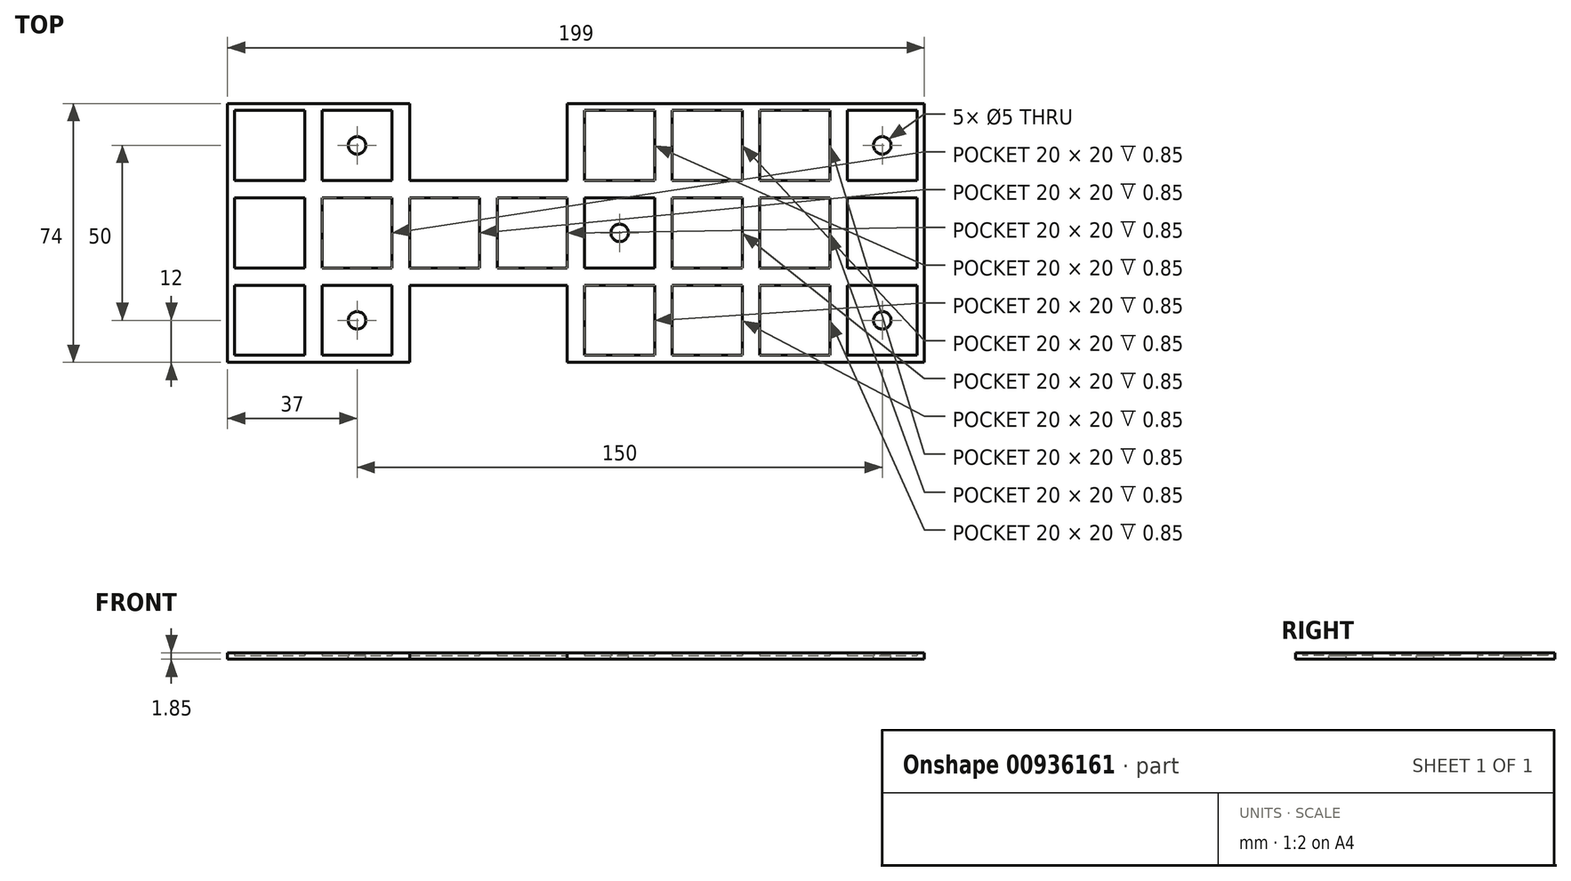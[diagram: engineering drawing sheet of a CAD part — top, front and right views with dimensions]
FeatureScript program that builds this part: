
annotation { "Feature Type Name" : "Feature", "Feature Type Description" : "" }
export const myFeature = defineFeature(function(context is Context, id is Id, definition is map)
    precondition{}
    {
        {
            var Q0;
            Q0=qCreatedBy(makeId("Top.planeOp"),FACE);
            var sketch = newSketch(context, id + "F0", { "sketchPlane" : qUnion([Q0])});
            skLineSegment(sketch, "E0.bottom", {"start": v(0, 0) * mm, "end": v(20, 0) * mm});
            skLineSegment(sketch, "E0.top", {"start": v(0, -20) * mm, "end": v(20, -20) * mm});
            skLineSegment(sketch, "E0.left", {"start": v(0, 0) * mm, "end": v(0, -20) * mm});
            skLineSegment(sketch, "E0.right", {"start": v(20, 0) * mm, "end": v(20, -20) * mm});
            skLineSegment(sketch, "E1.0.1.0", {"start": v(0, 25) * mm, "end": v(20, 25) * mm});
            skLineSegment(sketch, "E1.0.1.1", {"start": v(0, 25) * mm, "end": v(0, 5) * mm});
            skLineSegment(sketch, "E1.0.1.2", {"start": v(20, 25) * mm, "end": v(20, 5) * mm});
            skLineSegment(sketch, "E1.0.1.3", {"start": v(0, 5) * mm, "end": v(20, 5) * mm});
            skLineSegment(sketch, "E1.0.2.0", {"start": v(0, 50) * mm, "end": v(20, 50) * mm});
            skLineSegment(sketch, "E1.0.2.1", {"start": v(0, 50) * mm, "end": v(0, 30) * mm});
            skLineSegment(sketch, "E1.0.2.2", {"start": v(20, 50) * mm, "end": v(20, 30) * mm});
            skLineSegment(sketch, "E1.0.2.3", {"start": v(0, 30) * mm, "end": v(20, 30) * mm});
            skLineSegment(sketch, "E1.1.0.0", {"start": v(-25, 0) * mm, "end": v(-5, 0) * mm});
            skLineSegment(sketch, "E1.1.0.1", {"start": v(-25, 0) * mm, "end": v(-25, -20) * mm});
            skLineSegment(sketch, "E1.1.0.2", {"start": v(-5, 0) * mm, "end": v(-5, -20) * mm});
            skLineSegment(sketch, "E1.1.0.3", {"start": v(-25, -20) * mm, "end": v(-5, -20) * mm});
            skLineSegment(sketch, "E1.1.1.0", {"start": v(-25, 25) * mm, "end": v(-5, 25) * mm});
            skLineSegment(sketch, "E1.1.1.1", {"start": v(-25, 25) * mm, "end": v(-25, 5) * mm});
            skLineSegment(sketch, "E1.1.1.2", {"start": v(-5, 25) * mm, "end": v(-5, 5) * mm});
            skLineSegment(sketch, "E1.1.1.3", {"start": v(-25, 5) * mm, "end": v(-5, 5) * mm});
            skLineSegment(sketch, "E1.1.2.0", {"start": v(-25, 50) * mm, "end": v(-5, 50) * mm});
            skLineSegment(sketch, "E1.1.2.1", {"start": v(-25, 50) * mm, "end": v(-25, 30) * mm});
            skLineSegment(sketch, "E1.1.2.2", {"start": v(-5, 50) * mm, "end": v(-5, 30) * mm});
            skLineSegment(sketch, "E1.1.2.3", {"start": v(-25, 30) * mm, "end": v(-5, 30) * mm});
            skLineSegment(sketch, "E1.2.0.0", {"start": v(-50, 0) * mm, "end": v(-30, 0) * mm});
            skLineSegment(sketch, "E1.2.0.1", {"start": v(-50, 0) * mm, "end": v(-50, -20) * mm});
            skLineSegment(sketch, "E1.2.0.2", {"start": v(-30, 0) * mm, "end": v(-30, -20) * mm});
            skLineSegment(sketch, "E1.2.0.3", {"start": v(-50, -20) * mm, "end": v(-30, -20) * mm});
            skLineSegment(sketch, "E1.2.1.0", {"start": v(-50, 25) * mm, "end": v(-30, 25) * mm});
            skLineSegment(sketch, "E1.2.1.1", {"start": v(-50, 25) * mm, "end": v(-50, 5) * mm});
            skLineSegment(sketch, "E1.2.1.2", {"start": v(-30, 25) * mm, "end": v(-30, 5) * mm});
            skLineSegment(sketch, "E1.2.1.3", {"start": v(-50, 5) * mm, "end": v(-30, 5) * mm});
            skLineSegment(sketch, "E1.2.2.0", {"start": v(-50, 50) * mm, "end": v(-30, 50) * mm});
            skLineSegment(sketch, "E1.2.2.1", {"start": v(-50, 50) * mm, "end": v(-50, 30) * mm});
            skLineSegment(sketch, "E1.2.2.2", {"start": v(-30, 50) * mm, "end": v(-30, 30) * mm});
            skLineSegment(sketch, "E1.2.2.3", {"start": v(-50, 30) * mm, "end": v(-30, 30) * mm});
            skLineSegment(sketch, "E1.3.0.0", {"start": v(-75, 0) * mm, "end": v(-55, 0) * mm});
            skLineSegment(sketch, "E1.3.0.1", {"start": v(-75, 0) * mm, "end": v(-75, -20) * mm});
            skLineSegment(sketch, "E1.3.0.2", {"start": v(-55, 0) * mm, "end": v(-55, -20) * mm});
            skLineSegment(sketch, "E1.3.0.3", {"start": v(-75, -20) * mm, "end": v(-55, -20) * mm});
            skLineSegment(sketch, "E1.3.1.0", {"start": v(-75, 25) * mm, "end": v(-55, 25) * mm});
            skLineSegment(sketch, "E1.3.1.1", {"start": v(-75, 25) * mm, "end": v(-75, 5) * mm});
            skLineSegment(sketch, "E1.3.1.2", {"start": v(-55, 25) * mm, "end": v(-55, 5) * mm});
            skLineSegment(sketch, "E1.3.1.3", {"start": v(-75, 5) * mm, "end": v(-55, 5) * mm});
            skLineSegment(sketch, "E1.3.2.0", {"start": v(-75, 50) * mm, "end": v(-55, 50) * mm});
            skLineSegment(sketch, "E1.3.2.1", {"start": v(-75, 50) * mm, "end": v(-75, 30) * mm});
            skLineSegment(sketch, "E1.3.2.2", {"start": v(-55, 50) * mm, "end": v(-55, 30) * mm});
            skLineSegment(sketch, "E1.3.2.3", {"start": v(-75, 30) * mm, "end": v(-55, 30) * mm});
            skLineSegment(sketch, "E1.4.1.0", {"start": v(-100, 25) * mm, "end": v(-80, 25) * mm});
            skLineSegment(sketch, "E1.4.1.1", {"start": v(-100, 25) * mm, "end": v(-100, 5) * mm});
            skLineSegment(sketch, "E1.4.1.2", {"start": v(-80, 25) * mm, "end": v(-80, 5) * mm});
            skLineSegment(sketch, "E1.4.1.3", {"start": v(-100, 5) * mm, "end": v(-80, 5) * mm});
            skLineSegment(sketch, "E1.5.1.0", {"start": v(-125, 25) * mm, "end": v(-105, 25) * mm});
            skLineSegment(sketch, "E1.5.1.1", {"start": v(-125, 25) * mm, "end": v(-125, 5) * mm});
            skLineSegment(sketch, "E1.5.1.2", {"start": v(-105, 25) * mm, "end": v(-105, 5) * mm});
            skLineSegment(sketch, "E1.5.1.3", {"start": v(-125, 5) * mm, "end": v(-105, 5) * mm});
            skLineSegment(sketch, "E1.6.0.0", {"start": v(-150, 0) * mm, "end": v(-130, 0) * mm});
            skLineSegment(sketch, "E1.6.0.1", {"start": v(-150, 0) * mm, "end": v(-150, -20) * mm});
            skLineSegment(sketch, "E1.6.0.2", {"start": v(-130, 0) * mm, "end": v(-130, -20) * mm});
            skLineSegment(sketch, "E1.6.0.3", {"start": v(-150, -20) * mm, "end": v(-130, -20) * mm});
            skLineSegment(sketch, "E1.6.1.0", {"start": v(-150, 25) * mm, "end": v(-130, 25) * mm});
            skLineSegment(sketch, "E1.6.1.1", {"start": v(-150, 25) * mm, "end": v(-150, 5) * mm});
            skLineSegment(sketch, "E1.6.1.2", {"start": v(-130, 25) * mm, "end": v(-130, 5) * mm});
            skLineSegment(sketch, "E1.6.1.3", {"start": v(-150, 5) * mm, "end": v(-130, 5) * mm});
            skLineSegment(sketch, "E1.6.2.0", {"start": v(-150, 50) * mm, "end": v(-130, 50) * mm});
            skLineSegment(sketch, "E1.6.2.1", {"start": v(-150, 50) * mm, "end": v(-150, 30) * mm});
            skLineSegment(sketch, "E1.6.2.2", {"start": v(-130, 50) * mm, "end": v(-130, 30) * mm});
            skLineSegment(sketch, "E1.6.2.3", {"start": v(-150, 30) * mm, "end": v(-130, 30) * mm});
            skLineSegment(sketch, "E1.7.0.0", {"start": v(-175, 0) * mm, "end": v(-155, 0) * mm});
            skLineSegment(sketch, "E1.7.0.1", {"start": v(-175, 0) * mm, "end": v(-175, -20) * mm});
            skLineSegment(sketch, "E1.7.0.2", {"start": v(-155, 0) * mm, "end": v(-155, -20) * mm});
            skLineSegment(sketch, "E1.7.0.3", {"start": v(-175, -20) * mm, "end": v(-155, -20) * mm});
            skLineSegment(sketch, "E1.7.1.0", {"start": v(-175, 25) * mm, "end": v(-155, 25) * mm});
            skLineSegment(sketch, "E1.7.1.1", {"start": v(-175, 25) * mm, "end": v(-175, 5) * mm});
            skLineSegment(sketch, "E1.7.1.2", {"start": v(-155, 25) * mm, "end": v(-155, 5) * mm});
            skLineSegment(sketch, "E1.7.1.3", {"start": v(-175, 5) * mm, "end": v(-155, 5) * mm});
            skLineSegment(sketch, "E1.7.2.0", {"start": v(-175, 50) * mm, "end": v(-155, 50) * mm});
            skLineSegment(sketch, "E1.7.2.1", {"start": v(-175, 50) * mm, "end": v(-175, 30) * mm});
            skLineSegment(sketch, "E1.7.2.2", {"start": v(-155, 50) * mm, "end": v(-155, 30) * mm});
            skLineSegment(sketch, "E1.7.2.3", {"start": v(-175, 30) * mm, "end": v(-155, 30) * mm});
            skLineSegment(sketch, "E1.direction1", {"start": v(0, 0) * mm, "end": v(-25, 0) * mm, "construction": true});
            skLineSegment(sketch, "E1.direction2", {"start": v(0, 0) * mm, "end": v(0, 25) * mm, "construction": true});
            skLineSegment(sketch, "E2.bottom", {"start": v(-177, 52) * mm, "end": v(22, 52) * mm});
            skLineSegment(sketch, "E2.top", {"start": v(-177, -22) * mm, "end": v(22, -22) * mm});
            skLineSegment(sketch, "E2.left", {"start": v(-177, 52) * mm, "end": v(-177, -22) * mm});
            skLineSegment(sketch, "E2.right", {"start": v(22, 52) * mm, "end": v(22, -22) * mm});
            skLineSegment(sketch, "E3.bottom", {"start": v(-125, -22) * mm, "end": v(-80, -22) * mm});
            skLineSegment(sketch, "E3.top", {"start": v(-125, 0) * mm, "end": v(-80, 0) * mm});
            skLineSegment(sketch, "E3.left", {"start": v(-125, -22) * mm, "end": v(-125, 0) * mm});
            skLineSegment(sketch, "E3.right", {"start": v(-80, -22) * mm, "end": v(-80, 0) * mm});
            skLineSegment(sketch, "E4.bottom", {"start": v(-125, 52) * mm, "end": v(-80, 52) * mm});
            skLineSegment(sketch, "E4.top", {"start": v(-125, 30) * mm, "end": v(-80, 30) * mm});
            skLineSegment(sketch, "E4.left", {"start": v(-125, 52) * mm, "end": v(-125, 30) * mm});
            skLineSegment(sketch, "E4.right", {"start": v(-80, 52) * mm, "end": v(-80, 30) * mm});
            skPoint(sketch, "E5", {"position": v(10, -10) * mm});
            skPoint(sketch, "E5.positionSnap0", {"position": v(10, 0) * mm});
            skPoint(sketch, "E5.positionSnap1", {"position": v(20, -10) * mm});
            skPoint(sketch, "E6", {"position": v(10, 40) * mm});
            skPoint(sketch, "E6.positionSnap0", {"position": v(20, 40) * mm});
            skPoint(sketch, "E6.positionSnap1", {"position": v(10, 50) * mm});
            skPoint(sketch, "E7", {"position": v(-65, 15) * mm});
            skPoint(sketch, "E7.positionSnap0", {"position": v(-50, 15) * mm});
            skPoint(sketch, "E7.positionSnap1", {"position": v(-65, 25) * mm});
            skPoint(sketch, "E8", {"position": v(-140, -10) * mm});
            skPoint(sketch, "E8.positionSnap0", {"position": v(-140, 0) * mm});
            skPoint(sketch, "E8.positionSnap1", {"position": v(-130, -10) * mm});
            skPoint(sketch, "E9", {"position": v(-140, 40) * mm});
            skPoint(sketch, "E9.positionSnap0", {"position": v(-130, 40) * mm});
            skPoint(sketch, "E9.positionSnap1", {"position": v(-140, 50) * mm});
            skSolve(sketch);
        }
        {
            var Q0;
            Q0=makeQuery(id+"F0.imprint","IMPRINT",FACE,{"disambiguationData":[TD([[makeQuery(id+"F0.imprint","IMPRINT",EDGE,{"derivedFrom":sQuery(id+"F0.wireOp",EDGE,"E0.bottom")}),1.0]])]});
            extrude(context, id + "F1", {"entities" : qUnion([Q0]), "depth" : .85 * mm, "offsetDistance" : 25 * mm});
        }
        {
            var Q0;
            Q0=makeQuery(id+"F0.imprint","IMPRINT",FACE,{"disambiguationData":[TD([[makeQuery(id+"F0.imprint","IMPRINT",EDGE,{"derivedFrom":sQuery(id+"F0.wireOp",EDGE,"E1.6.1.0")}),-1.0]])]});
            var Q1;
            Q1=makeQuery(id+"F0.imprint","IMPRINT",FACE,{"disambiguationData":[TD([[makeQuery(id+"F0.imprint","IMPRINT",EDGE,{"derivedFrom":sQuery(id+"F0.wireOp",EDGE,"E1.7.1.0")}),-1.0]])]});
            var Q2;
            Q2=makeQuery(id+"F0.imprint","IMPRINT",FACE,{"disambiguationData":[TD([[makeQuery(id+"F0.imprint","IMPRINT",EDGE,{"derivedFrom":sQuery(id+"F0.wireOp",EDGE,"E1.7.2.0")}),-1.0]])]});
            var Q3;
            Q3=makeQuery(id+"F0.imprint","IMPRINT",FACE,{"disambiguationData":[TD([[makeQuery(id+"F0.imprint","IMPRINT",EDGE,{"derivedFrom":sQuery(id+"F0.wireOp",EDGE,"E1.6.2.0")}),-1.0]])]});
            var Q4;
            Q4=makeQuery(id+"F0.imprint","IMPRINT",FACE,{"disambiguationData":[TD([[makeQuery(id+"F0.imprint","IMPRINT",EDGE,{"derivedFrom":sQuery(id+"F0.wireOp",EDGE,"E1.5.1.0")}),-1.0]])]});
            var Q5;
            Q5=makeQuery(id+"F0.imprint","IMPRINT",FACE,{"disambiguationData":[TD([[makeQuery(id+"F0.imprint","IMPRINT",EDGE,{"derivedFrom":sQuery(id+"F0.wireOp",EDGE,"E1.6.0.0")}),-1.0]])]});
            var Q6;
            Q6=makeQuery(id+"F0.imprint","IMPRINT",FACE,{"disambiguationData":[TD([[makeQuery(id+"F0.imprint","IMPRINT",EDGE,{"derivedFrom":sQuery(id+"F0.wireOp",EDGE,"E1.7.0.0")}),-1.0]])]});
            var Q7;
            Q7=makeQuery(id+"F0.imprint","IMPRINT",FACE,{"disambiguationData":[TD([[makeQuery(id+"F0.imprint","IMPRINT",EDGE,{"derivedFrom":sQuery(id+"F0.wireOp",EDGE,"E1.4.1.0")}),-1.0]])]});
            var Q8;
            Q8=makeQuery(id+"F0.imprint","IMPRINT",FACE,{"disambiguationData":[TD([[makeQuery(id+"F0.imprint","IMPRINT",EDGE,{"derivedFrom":sQuery(id+"F0.wireOp",EDGE,"E1.3.2.0")}),-1.0]])]});
            var Q9;
            Q9=makeQuery(id+"F0.imprint","IMPRINT",FACE,{"disambiguationData":[TD([[makeQuery(id+"F0.imprint","IMPRINT",EDGE,{"derivedFrom":sQuery(id+"F0.wireOp",EDGE,"E1.3.1.0")}),-1.0]])]});
            var Q10;
            Q10=makeQuery(id+"F0.imprint","IMPRINT",FACE,{"disambiguationData":[TD([[makeQuery(id+"F0.imprint","IMPRINT",EDGE,{"derivedFrom":sQuery(id+"F0.wireOp",EDGE,"E1.2.1.0")}),-1.0]])]});
            var Q11;
            Q11=makeQuery(id+"F0.imprint","IMPRINT",FACE,{"disambiguationData":[TD([[makeQuery(id+"F0.imprint","IMPRINT",EDGE,{"derivedFrom":sQuery(id+"F0.wireOp",EDGE,"E1.3.0.0")}),-1.0]])]});
            var Q12;
            Q12=makeQuery(id+"F0.imprint","IMPRINT",FACE,{"disambiguationData":[TD([[makeQuery(id+"F0.imprint","IMPRINT",EDGE,{"derivedFrom":sQuery(id+"F0.wireOp",EDGE,"E1.2.0.0")}),-1.0]])]});
            var Q13;
            Q13=makeQuery(id+"F0.imprint","IMPRINT",FACE,{"disambiguationData":[TD([[makeQuery(id+"F0.imprint","IMPRINT",EDGE,{"derivedFrom":sQuery(id+"F0.wireOp",EDGE,"E1.2.2.0")}),-1.0]])]});
            var Q14;
            Q14=makeQuery(id+"F0.imprint","IMPRINT",FACE,{"disambiguationData":[TD([[makeQuery(id+"F0.imprint","IMPRINT",EDGE,{"derivedFrom":sQuery(id+"F0.wireOp",EDGE,"E1.1.2.0")}),-1.0]])]});
            var Q15;
            Q15=makeQuery(id+"F0.imprint","IMPRINT",FACE,{"disambiguationData":[TD([[makeQuery(id+"F0.imprint","IMPRINT",EDGE,{"derivedFrom":sQuery(id+"F0.wireOp",EDGE,"E1.1.1.0")}),-1.0]])]});
            var Q16;
            Q16=makeQuery(id+"F0.imprint","IMPRINT",FACE,{"disambiguationData":[TD([[makeQuery(id+"F0.imprint","IMPRINT",EDGE,{"derivedFrom":sQuery(id+"F0.wireOp",EDGE,"E1.1.0.0")}),-1.0]])]});
            var Q17;
            Q17=makeQuery(id+"F0.imprint","IMPRINT",FACE,{"disambiguationData":[TD([[makeQuery(id+"F0.imprint","IMPRINT",EDGE,{"derivedFrom":sQuery(id+"F0.wireOp",EDGE,"E0.bottom")}),-1.0]])]});
            var Q18;
            Q18=makeQuery(id+"F0.imprint","IMPRINT",FACE,{"disambiguationData":[TD([[makeQuery(id+"F0.imprint","IMPRINT",EDGE,{"derivedFrom":sQuery(id+"F0.wireOp",EDGE,"E1.0.1.0")}),-1.0]])]});
            var Q19;
            Q19=makeQuery(id+"F0.imprint","IMPRINT",FACE,{"disambiguationData":[TD([[makeQuery(id+"F0.imprint","IMPRINT",EDGE,{"derivedFrom":sQuery(id+"F0.wireOp",EDGE,"E1.0.2.0")}),-1.0]])]});
            var Q20;
            Q20=makeQuery(id+"F1.opExtrude","CAP_FACE",FACE,{"disambiguationData":[OSD([sQuery(id+"F0.wireOp",EDGE,"E0.bottom"),sQuery(id+"F0.wireOp",EDGE,"E0.top"),sQuery(id+"F0.wireOp",EDGE,"E0.left"),sQuery(id+"F0.wireOp",EDGE,"E0.right"),sQuery(id+"F0.wireOp",EDGE,"E1.0.1.0"),sQuery(id+"F0.wireOp",EDGE,"E1.0.1.1"),sQuery(id+"F0.wireOp",EDGE,"E1.0.1.2"),sQuery(id+"F0.wireOp",EDGE,"E1.0.1.3"),sQuery(id+"F0.wireOp",EDGE,"E1.0.2.0"),sQuery(id+"F0.wireOp",EDGE,"E1.0.2.1"),sQuery(id+"F0.wireOp",EDGE,"E1.0.2.2"),sQuery(id+"F0.wireOp",EDGE,"E1.0.2.3"),sQuery(id+"F0.wireOp",EDGE,"E1.1.0.0"),sQuery(id+"F0.wireOp",EDGE,"E1.1.0.1"),sQuery(id+"F0.wireOp",EDGE,"E1.1.0.2"),sQuery(id+"F0.wireOp",EDGE,"E1.1.0.3"),sQuery(id+"F0.wireOp",EDGE,"E1.1.1.0"),sQuery(id+"F0.wireOp",EDGE,"E1.1.1.1"),sQuery(id+"F0.wireOp",EDGE,"E1.1.1.2"),sQuery(id+"F0.wireOp",EDGE,"E1.1.1.3"),sQuery(id+"F0.wireOp",EDGE,"E1.1.2.0"),sQuery(id+"F0.wireOp",EDGE,"E1.1.2.1"),sQuery(id+"F0.wireOp",EDGE,"E1.1.2.2"),sQuery(id+"F0.wireOp",EDGE,"E1.1.2.3"),sQuery(id+"F0.wireOp",EDGE,"E1.2.0.0"),sQuery(id+"F0.wireOp",EDGE,"E1.2.0.1"),sQuery(id+"F0.wireOp",EDGE,"E1.2.0.2"),sQuery(id+"F0.wireOp",EDGE,"E1.2.0.3"),sQuery(id+"F0.wireOp",EDGE,"E1.2.1.0"),sQuery(id+"F0.wireOp",EDGE,"E1.2.1.1"),sQuery(id+"F0.wireOp",EDGE,"E1.2.1.2"),sQuery(id+"F0.wireOp",EDGE,"E1.2.1.3"),sQuery(id+"F0.wireOp",EDGE,"E1.2.2.0"),sQuery(id+"F0.wireOp",EDGE,"E1.2.2.1"),sQuery(id+"F0.wireOp",EDGE,"E1.2.2.2"),sQuery(id+"F0.wireOp",EDGE,"E1.2.2.3"),sQuery(id+"F0.wireOp",EDGE,"E1.3.0.0"),sQuery(id+"F0.wireOp",EDGE,"E1.3.0.1"),sQuery(id+"F0.wireOp",EDGE,"E1.3.0.2"),sQuery(id+"F0.wireOp",EDGE,"E1.3.0.3"),sQuery(id+"F0.wireOp",EDGE,"E1.3.1.0"),sQuery(id+"F0.wireOp",EDGE,"E1.3.1.1"),sQuery(id+"F0.wireOp",EDGE,"E1.3.1.2"),sQuery(id+"F0.wireOp",EDGE,"E1.3.1.3"),sQuery(id+"F0.wireOp",EDGE,"E1.3.2.0"),sQuery(id+"F0.wireOp",EDGE,"E1.3.2.1"),sQuery(id+"F0.wireOp",EDGE,"E1.3.2.2"),sQuery(id+"F0.wireOp",EDGE,"E1.3.2.3"),sQuery(id+"F0.wireOp",EDGE,"E1.4.1.0"),sQuery(id+"F0.wireOp",EDGE,"E1.4.1.1"),sQuery(id+"F0.wireOp",EDGE,"E1.4.1.2"),sQuery(id+"F0.wireOp",EDGE,"E1.4.1.3"),sQuery(id+"F0.wireOp",EDGE,"E1.5.1.0"),sQuery(id+"F0.wireOp",EDGE,"E1.5.1.1"),sQuery(id+"F0.wireOp",EDGE,"E1.5.1.2"),sQuery(id+"F0.wireOp",EDGE,"E1.5.1.3"),sQuery(id+"F0.wireOp",EDGE,"E1.6.0.0"),sQuery(id+"F0.wireOp",EDGE,"E1.6.0.1"),sQuery(id+"F0.wireOp",EDGE,"E1.6.0.2"),sQuery(id+"F0.wireOp",EDGE,"E1.6.0.3"),sQuery(id+"F0.wireOp",EDGE,"E1.6.1.0"),sQuery(id+"F0.wireOp",EDGE,"E1.6.1.1"),sQuery(id+"F0.wireOp",EDGE,"E1.6.1.2"),sQuery(id+"F0.wireOp",EDGE,"E1.6.1.3"),sQuery(id+"F0.wireOp",EDGE,"E1.6.2.0"),sQuery(id+"F0.wireOp",EDGE,"E1.6.2.1"),sQuery(id+"F0.wireOp",EDGE,"E1.6.2.2"),sQuery(id+"F0.wireOp",EDGE,"E1.6.2.3"),sQuery(id+"F0.wireOp",EDGE,"E1.7.0.0"),sQuery(id+"F0.wireOp",EDGE,"E1.7.0.1"),sQuery(id+"F0.wireOp",EDGE,"E1.7.0.2"),sQuery(id+"F0.wireOp",EDGE,"E1.7.0.3"),sQuery(id+"F0.wireOp",EDGE,"E1.7.1.0"),sQuery(id+"F0.wireOp",EDGE,"E1.7.1.1"),sQuery(id+"F0.wireOp",EDGE,"E1.7.1.2"),sQuery(id+"F0.wireOp",EDGE,"E1.7.1.3"),sQuery(id+"F0.wireOp",EDGE,"E1.7.2.0"),sQuery(id+"F0.wireOp",EDGE,"E1.7.2.1"),sQuery(id+"F0.wireOp",EDGE,"E1.7.2.2"),sQuery(id+"F0.wireOp",EDGE,"E1.7.2.3"),sQuery(id+"F0.wireOp",EDGE,"E2.bottom"),sQuery(id+"F0.wireOp",EDGE,"E2.top"),sQuery(id+"F0.wireOp",EDGE,"E2.left"),sQuery(id+"F0.wireOp",EDGE,"E2.right"),sQuery(id+"F0.wireOp",EDGE,"E3.top"),sQuery(id+"F0.wireOp",EDGE,"E3.left"),sQuery(id+"F0.wireOp",EDGE,"E3.right"),sQuery(id+"F0.wireOp",EDGE,"E4.top"),sQuery(id+"F0.wireOp",EDGE,"E4.left"),sQuery(id+"F0.wireOp",EDGE,"E4.right")])],"isStart":false});
            var Q21;
            Q21=makeQuery(id+"F0.imprint","IMPRINT",FACE,{"disambiguationData":[TD([[makeQuery(id+"F0.imprint","IMPRINT",EDGE,{"derivedFrom":sQuery(id+"F0.wireOp",EDGE,"E0.bottom")}),1.0]])]});
            extrude(context, id + "F2", {"entities" : qUnion([Q0, Q1, Q2, Q3, Q4, Q5, Q6, Q7, Q8, Q9, Q10, Q11, Q12, Q13, Q14, Q15, Q16, Q17, Q18, Q19, Q20, Q21]), "operationType" : NewBodyOperationType.ADD, "oppositeDirection" : true, "depth" : 1 * mm, "offsetDistance" : 25 * mm});
        }
        {
            var Q0;
            Q0=sQuery(id+"F0.wireOp",VERTEX,"E9");
            var Q1;
            Q1=sQuery(id+"F0.wireOp",VERTEX,"E8");
            var Q2;
            Q2=sQuery(id+"F0.wireOp",VERTEX,"E7");
            var Q3;
            Q3=sQuery(id+"F0.wireOp",VERTEX,"E5");
            var Q4;
            Q4=sQuery(id+"F0.wireOp",VERTEX,"E6");
            var Q5;
            Q5=makeQuery(id+"F1.opExtrude","SWEPT_BODY",BODY,{"disambiguationData":[OSD([sQuery(id+"F0.wireOp",EDGE,"E0.bottom"),sQuery(id+"F0.wireOp",EDGE,"E0.top"),sQuery(id+"F0.wireOp",EDGE,"E0.left"),sQuery(id+"F0.wireOp",EDGE,"E0.right"),sQuery(id+"F0.wireOp",EDGE,"E1.0.1.0"),sQuery(id+"F0.wireOp",EDGE,"E1.0.1.1"),sQuery(id+"F0.wireOp",EDGE,"E1.0.1.2"),sQuery(id+"F0.wireOp",EDGE,"E1.0.1.3"),sQuery(id+"F0.wireOp",EDGE,"E1.0.2.0"),sQuery(id+"F0.wireOp",EDGE,"E1.0.2.1"),sQuery(id+"F0.wireOp",EDGE,"E1.0.2.2"),sQuery(id+"F0.wireOp",EDGE,"E1.0.2.3"),sQuery(id+"F0.wireOp",EDGE,"E1.1.0.0"),sQuery(id+"F0.wireOp",EDGE,"E1.1.0.1"),sQuery(id+"F0.wireOp",EDGE,"E1.1.0.2"),sQuery(id+"F0.wireOp",EDGE,"E1.1.0.3"),sQuery(id+"F0.wireOp",EDGE,"E1.1.1.0"),sQuery(id+"F0.wireOp",EDGE,"E1.1.1.1"),sQuery(id+"F0.wireOp",EDGE,"E1.1.1.2"),sQuery(id+"F0.wireOp",EDGE,"E1.1.1.3"),sQuery(id+"F0.wireOp",EDGE,"E1.1.2.0"),sQuery(id+"F0.wireOp",EDGE,"E1.1.2.1"),sQuery(id+"F0.wireOp",EDGE,"E1.1.2.2"),sQuery(id+"F0.wireOp",EDGE,"E1.1.2.3"),sQuery(id+"F0.wireOp",EDGE,"E1.2.0.0"),sQuery(id+"F0.wireOp",EDGE,"E1.2.0.1"),sQuery(id+"F0.wireOp",EDGE,"E1.2.0.2"),sQuery(id+"F0.wireOp",EDGE,"E1.2.0.3"),sQuery(id+"F0.wireOp",EDGE,"E1.2.1.0"),sQuery(id+"F0.wireOp",EDGE,"E1.2.1.1"),sQuery(id+"F0.wireOp",EDGE,"E1.2.1.2"),sQuery(id+"F0.wireOp",EDGE,"E1.2.1.3"),sQuery(id+"F0.wireOp",EDGE,"E1.2.2.0"),sQuery(id+"F0.wireOp",EDGE,"E1.2.2.1"),sQuery(id+"F0.wireOp",EDGE,"E1.2.2.2"),sQuery(id+"F0.wireOp",EDGE,"E1.2.2.3"),sQuery(id+"F0.wireOp",EDGE,"E1.3.0.0"),sQuery(id+"F0.wireOp",EDGE,"E1.3.0.1"),sQuery(id+"F0.wireOp",EDGE,"E1.3.0.2"),sQuery(id+"F0.wireOp",EDGE,"E1.3.0.3"),sQuery(id+"F0.wireOp",EDGE,"E1.3.1.0"),sQuery(id+"F0.wireOp",EDGE,"E1.3.1.1"),sQuery(id+"F0.wireOp",EDGE,"E1.3.1.2"),sQuery(id+"F0.wireOp",EDGE,"E1.3.1.3"),sQuery(id+"F0.wireOp",EDGE,"E1.3.2.0"),sQuery(id+"F0.wireOp",EDGE,"E1.3.2.1"),sQuery(id+"F0.wireOp",EDGE,"E1.3.2.2"),sQuery(id+"F0.wireOp",EDGE,"E1.3.2.3"),sQuery(id+"F0.wireOp",EDGE,"E1.4.1.0"),sQuery(id+"F0.wireOp",EDGE,"E1.4.1.1"),sQuery(id+"F0.wireOp",EDGE,"E1.4.1.2"),sQuery(id+"F0.wireOp",EDGE,"E1.4.1.3"),sQuery(id+"F0.wireOp",EDGE,"E1.5.1.0"),sQuery(id+"F0.wireOp",EDGE,"E1.5.1.1"),sQuery(id+"F0.wireOp",EDGE,"E1.5.1.2"),sQuery(id+"F0.wireOp",EDGE,"E1.5.1.3"),sQuery(id+"F0.wireOp",EDGE,"E1.6.0.0"),sQuery(id+"F0.wireOp",EDGE,"E1.6.0.1"),sQuery(id+"F0.wireOp",EDGE,"E1.6.0.2"),sQuery(id+"F0.wireOp",EDGE,"E1.6.0.3"),sQuery(id+"F0.wireOp",EDGE,"E1.6.1.0"),sQuery(id+"F0.wireOp",EDGE,"E1.6.1.1"),sQuery(id+"F0.wireOp",EDGE,"E1.6.1.2"),sQuery(id+"F0.wireOp",EDGE,"E1.6.1.3"),sQuery(id+"F0.wireOp",EDGE,"E1.6.2.0"),sQuery(id+"F0.wireOp",EDGE,"E1.6.2.1"),sQuery(id+"F0.wireOp",EDGE,"E1.6.2.2"),sQuery(id+"F0.wireOp",EDGE,"E1.6.2.3"),sQuery(id+"F0.wireOp",EDGE,"E1.7.0.0"),sQuery(id+"F0.wireOp",EDGE,"E1.7.0.1"),sQuery(id+"F0.wireOp",EDGE,"E1.7.0.2"),sQuery(id+"F0.wireOp",EDGE,"E1.7.0.3"),sQuery(id+"F0.wireOp",EDGE,"E1.7.1.0"),sQuery(id+"F0.wireOp",EDGE,"E1.7.1.1"),sQuery(id+"F0.wireOp",EDGE,"E1.7.1.2"),sQuery(id+"F0.wireOp",EDGE,"E1.7.1.3"),sQuery(id+"F0.wireOp",EDGE,"E1.7.2.0"),sQuery(id+"F0.wireOp",EDGE,"E1.7.2.1"),sQuery(id+"F0.wireOp",EDGE,"E1.7.2.2"),sQuery(id+"F0.wireOp",EDGE,"E1.7.2.3"),sQuery(id+"F0.wireOp",EDGE,"E2.bottom"),sQuery(id+"F0.wireOp",EDGE,"E2.top"),sQuery(id+"F0.wireOp",EDGE,"E2.left"),sQuery(id+"F0.wireOp",EDGE,"E2.right"),sQuery(id+"F0.wireOp",EDGE,"E3.top"),sQuery(id+"F0.wireOp",EDGE,"E3.left"),sQuery(id+"F0.wireOp",EDGE,"E3.right"),sQuery(id+"F0.wireOp",EDGE,"E4.top"),sQuery(id+"F0.wireOp",EDGE,"E4.left"),sQuery(id+"F0.wireOp",EDGE,"E4.right")])]});
            hole(context, id + "F3", {"style" : HoleStyle.SIMPLE, "endStyle" : HoleEndStyle.THROUGH, "holeDiameter" : 5 * mm, "majorDiameter" : 5 * mm, "isTappedThrough" : true, "tappedDepth" : 12 * mm, "tapClearance" : 3, "locations" : qUnion([Q0, Q1, Q2, Q3, Q4]), "scope" : qUnion([Q5])});
        }
    });
